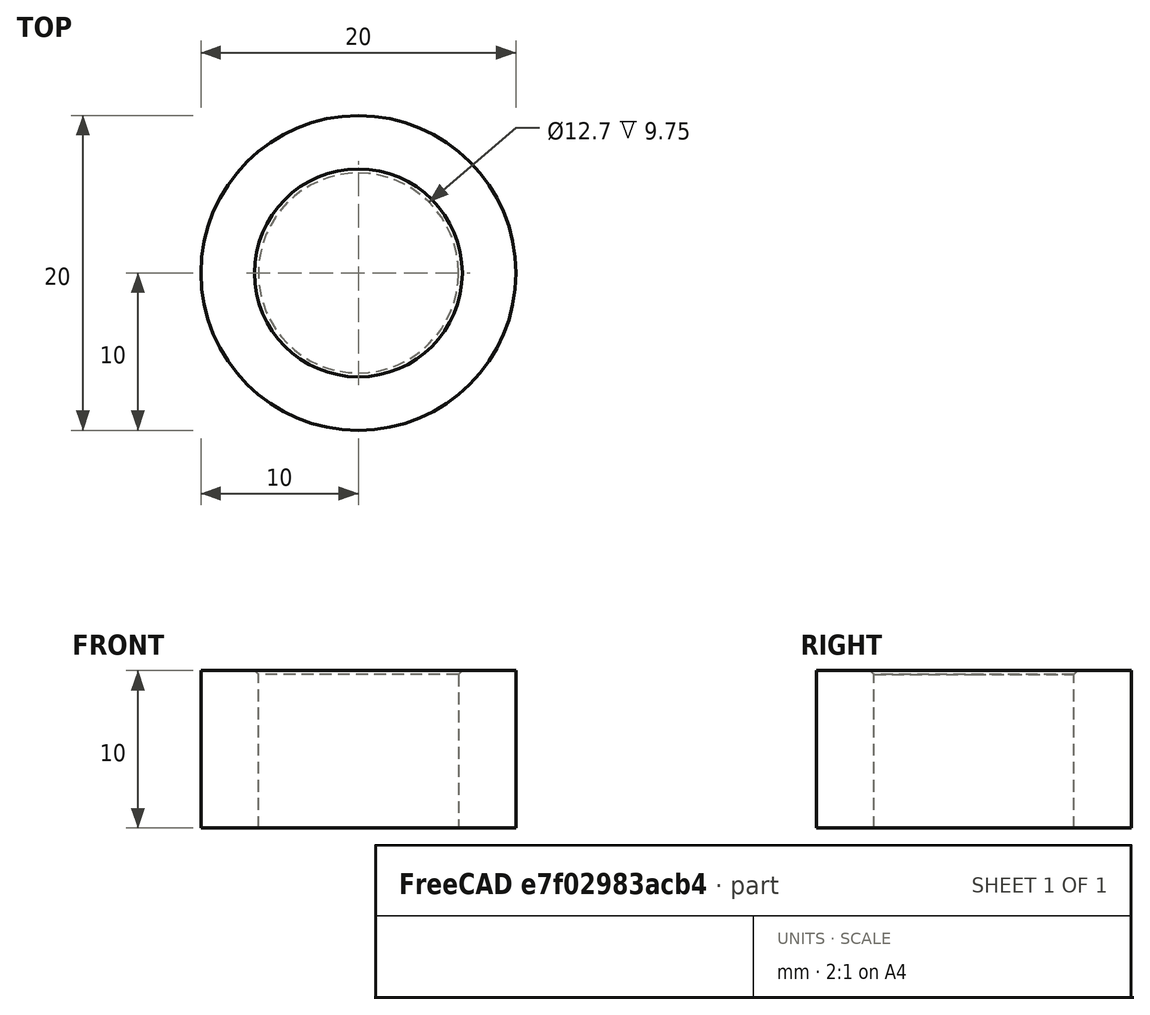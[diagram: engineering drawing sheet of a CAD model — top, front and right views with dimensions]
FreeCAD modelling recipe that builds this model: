
FCSTD DOCUMENT  (FreeCAD 0.16R)
Label: AxleSpacers
License: All rights reserved
LicenseURL: http://en.wikipedia.org/wiki/All_rights_reserved
objects: Sketcher::SketchObject×2, PartDesign::Pad×1, PartDesign::Pocket×1, PartDesign::Chamfer×1, Mesh::Feature×1
note: 7 computed .brp shape members not serialized (recipe doc carries the construction recipe); baked Part::Feature solids carry a one-line shape summary decoded from their .brp

FEATURE [Sketcher::SketchObject] Sketch
  sketch-geometry (1):
    g0: Circle CenterX=0 CenterY=0 CenterZ=0 NormalX=0 NormalY=0 NormalZ=1 Radius=10
  constraints (2):
    c: Coincident(g0,g-1)
    c: Radius(g0) = 10
FEATURE [PartDesign::Pad] Pad
  Length = 10
  Length2 = 100
  Sketch = -> Sketch
  Type = 0
FEATURE [Sketcher::SketchObject] Sketch001
  Placement = pos=(0,0,10) rot=(0,0,1;0rad)
  Support = -> Pad [Face3]
  sketch-geometry (1):
    g0: Circle CenterX=0 CenterY=0 CenterZ=0 NormalX=0 NormalY=0 NormalZ=1 Radius=6.35
  constraints (2):
    c: Coincident(g0,g-1)
    c: Radius(g0) = 6.35
FEATURE [PartDesign::Pocket] Pocket
  Length = 5
  Sketch = -> Sketch001
  Type = 1
FEATURE [PartDesign::Chamfer] Chamfer
  Base = -> Pocket [Edge5]
  Size = 0.25
FEATURE [Mesh::Feature] Mesh  label="Chamfer (Meshed)"
